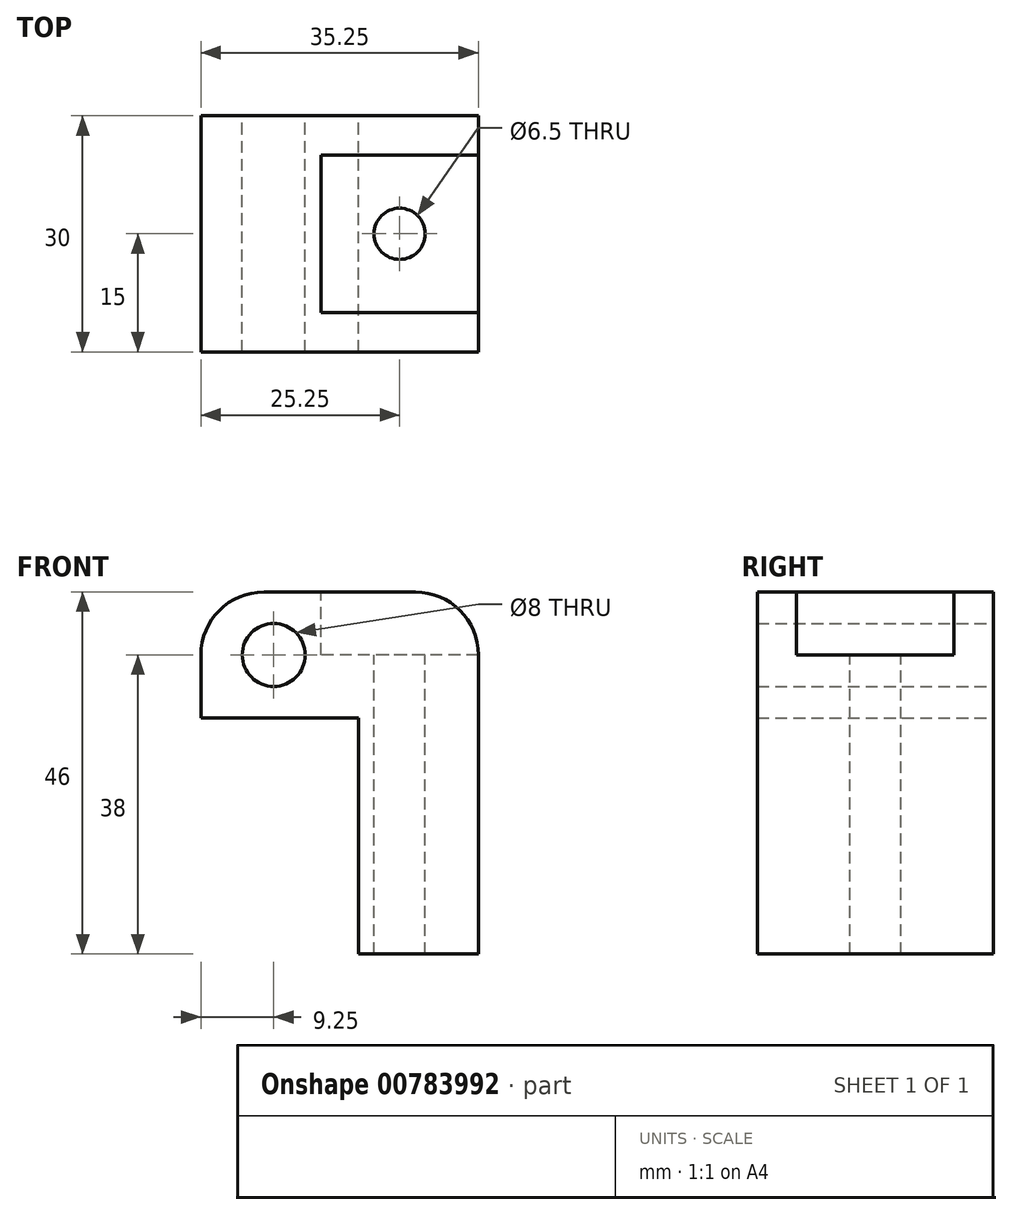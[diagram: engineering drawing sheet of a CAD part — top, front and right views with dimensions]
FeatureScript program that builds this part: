
annotation { "Feature Type Name" : "Feature", "Feature Type Description" : "" }
export const myFeature = defineFeature(function(context is Context, id is Id, definition is map)
    precondition{}
    {
        {
            var Q0;
            Q0=qCreatedBy(makeId("Front.planeOp"),FACE);
            var sketch = newSketch(context, id + "F0", { "sketchPlane" : qUnion([Q0])});
            skLineSegment(sketch, "E0", {"start": v(0, 0) * mm, "end": v(0, -30) * mm});
            skLineSegment(sketch, "E1", {"start": v(0, -30) * mm, "end": v(15.25, -30) * mm});
            skLineSegment(sketch, "E2", {"start": v(15.25, -30) * mm, "end": v(15.25, 16) * mm});
            skLineSegment(sketch, "E3", {"start": v(15.25, 16) * mm, "end": v(-20, 16) * mm});
            skLineSegment(sketch, "E4", {"start": v(-20, 16) * mm, "end": v(-20, 0) * mm});
            skLineSegment(sketch, "E5", {"start": v(-20, 0) * mm, "end": v(0, 0) * mm});
            skCircle(sketch, "E6", {"center": v(-10.75, 8) * mm, "radius": 4 * mm});
            skPoint(sketch, "E6.centerSnap0", {"position": v(-20, 8) * mm});
            skLineSegment(sketch, "E7", {"start": v(15.25, 8) * mm, "end": v(-4.75, 8) * mm});
            skLineSegment(sketch, "E8", {"start": v(-4.75, 8) * mm, "end": v(-4.75, 16) * mm});
            skPoint(sketch, "E9", {"position": v(5.25, 8) * mm});
            skSolve(sketch);
        }
        {
            var Q0;
            Q0=makeQuery(id+"F0.imprint","IMPRINT",FACE,{"disambiguationData":[TD([[makeQuery(id+"F0.imprint","IMPRINT",EDGE,{"derivedFrom":sQuery(id+"F0.wireOp",EDGE,"E0")}),1.0]])]});
            var Q1;
            {var subQ3=sQuery(id+"F0.wireOp",EDGE,"E7");Q1=makeQuery(id+"F0.imprint","IMPRINT",FACE,{"disambiguationData":[TD([[makeQuery(id+"F0.imprint","IMPRINT",EDGE,{"derivedFrom":subQ3}),-1.0]])]});}
            extrude(context, id + "F1", {"entities" : qUnion([Q0, Q1]), "endBound" : BoundingType.SYMMETRIC, "depth" : 30 * mm, "offsetDistance" : 25 * mm});
        }
        {
            var Q0;
            {var subQ3=sQuery(id+"F0.wireOp",EDGE,"E7");Q0=makeQuery(id+"F0.imprint","IMPRINT",FACE,{"disambiguationData":[TD([[makeQuery(id+"F0.imprint","IMPRINT",EDGE,{"derivedFrom":subQ3}),-1.0]])]});}
            extrude(context, id + "F2", {"entities" : qUnion([Q0]), "operationType" : NewBodyOperationType.REMOVE, "endBound" : BoundingType.SYMMETRIC, "depth" : 20 * mm, "offsetDistance" : 25 * mm});
        }
        {
            var Q0;
            Q0=makeQuery(id+"F2.boolean.opBoolean","COPY",FACE,{"derivedFrom":makeQuery(id+"F2.opExtrude","SWEPT_FACE",FACE,{"disambiguationData":[OSD([sQuery(id+"F0.wireOp",EDGE,"E7")])]})});
            var sketch = newSketch(context, id + "F3", { "sketchPlane" : qUnion([Q0])});
            skPoint(sketch, "E10", {"position": v(5.25, 0) * mm});
            skPoint(sketch, "E10.positionSnap0", {"position": v(5.25, 10) * mm});
            skPoint(sketch, "E10.positionSnap1", {"position": v(15.25, 0) * mm});
            skCircle(sketch, "E11", {"center": v(5.25, 0) * mm, "radius": 3.25 * mm});
            skSolve(sketch);
        }
        {
            var Q0;
            Q0=makeQuery(id+"F3.imprint","IMPRINT",FACE,{"disambiguationData":[TD([[makeQuery(id+"F3.imprint","IMPRINT",EDGE,{"derivedFrom":sQuery(id+"F3.wireOp",EDGE,"E11")}),1.0]])]});
            extrude(context, id + "F4", {"entities" : qUnion([Q0]), "operationType" : NewBodyOperationType.REMOVE, "endBound" : BoundingType.THROUGH_ALL, "oppositeDirection" : true, "depth" : 25 * mm, "offsetDistance" : 25 * mm});
        }
        {
            var Q0;
            Q0=makeQuery(id+"F1.opExtrude","SWEPT_EDGE",EDGE,{"disambiguationData":[OSD([sQuery(id+"F0.wireOp",EDGE,"E3"),sQuery(id+"F0.wireOp",EDGE,"E4")])]});
            var Q1;
            {var subQ0=sQuery(id+"F0.wireOp",EDGE,"E3");var subQ1=sQuery(id+"F0.wireOp",EDGE,"E2");Q1=makeQuery(id+"F2.boolean.opBoolean","SPLIT",EDGE,{"disambiguationData":[TD([makeQuery(id+"F2.opExtrude","CAP_FACE",FACE,{"disambiguationData":[OSD([subQ1,subQ0,sQuery(id+"F0.wireOp",EDGE,"E7"),sQuery(id+"F0.wireOp",EDGE,"E8")])],"isStart":false})])],"derivedFrom":makeQuery(id+"F1.opExtrude","SWEPT_EDGE",EDGE,{"disambiguationData":[OSD([subQ1,subQ0])]})});}
            var Q2;
            {var subQ0=sQuery(id+"F0.wireOp",EDGE,"E3");var subQ1=sQuery(id+"F0.wireOp",EDGE,"E2");Q2=makeQuery(id+"F2.boolean.opBoolean","SPLIT",EDGE,{"disambiguationData":[TD([makeQuery(id+"F2.opExtrude","CAP_FACE",FACE,{"disambiguationData":[OSD([subQ1,subQ0,sQuery(id+"F0.wireOp",EDGE,"E7"),sQuery(id+"F0.wireOp",EDGE,"E8")])],"isStart":true})])],"derivedFrom":makeQuery(id+"F1.opExtrude","SWEPT_EDGE",EDGE,{"disambiguationData":[OSD([subQ1,subQ0])]})});}
            fillet(context, id + "F5", {"entities" : qUnion([Q0, Q1, Q2]), "radius" : 8 * mm, "tangentPropagation" : true, "allowEdgeOverflow" : false});
        }
    });
